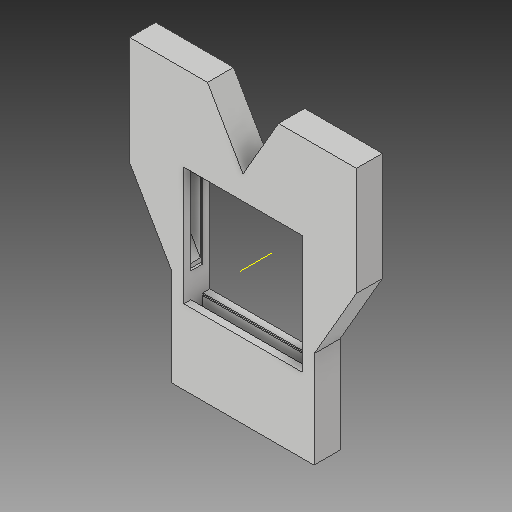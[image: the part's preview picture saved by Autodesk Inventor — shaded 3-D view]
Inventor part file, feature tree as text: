
AUTODESK INVENTOR PART (.ipt)
format: ipt  version: 2017 (Build 210142000, 142)  size: 177,152 bytes
history: native  units: in
note: dims shown in document units (in); Inventor stores cm internally (conversion verified against a paired STEP export)
features: other x4, plane x1, sketch x1
ambient origin geometry x8: Origin, YZ Plane, XZ Plane, XY Plane, X Axis, Y Axis, Z Axis, Center Point
bodies: Solid1 (feature_tree)
feature tree (6):
  other  "end door frame (100).ipt"
  plane  "Work Plane1"
  sketch  "Sketch1"  dims[d0=0.0354in d1=4.5in]
  other  "mate for doors"
  other  "rame of door::end door frame (100).ipt"
  other  "TaggingFeature1"
